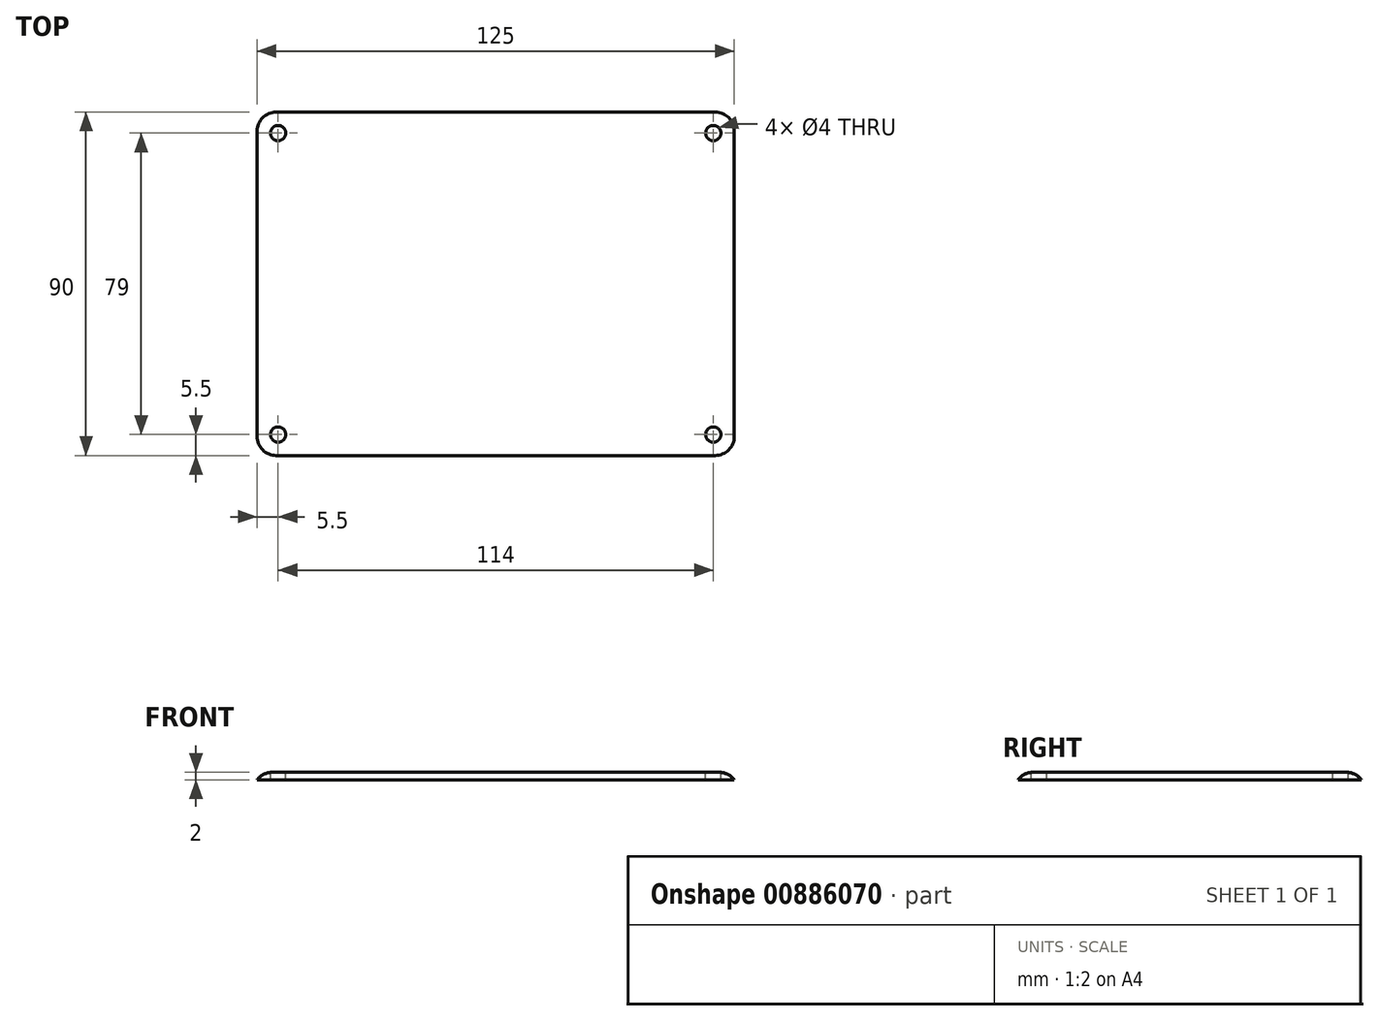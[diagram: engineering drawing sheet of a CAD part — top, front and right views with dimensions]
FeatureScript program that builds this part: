
annotation { "Feature Type Name" : "Feature", "Feature Type Description" : "" }
export const myFeature = defineFeature(function(context is Context, id is Id, definition is map)
    precondition{}
    {
        {
            var Q0;
            Q0=qCreatedBy(makeId("Top.planeOp"),FACE);
            var sketch = newSketch(context, id + "F0", { "sketchPlane" : qUnion([Q0])});
            skLineSegment(sketch, "E0.bottom", {"start": v(62.5, -45) * mm, "end": v(-62.5, -45) * mm});
            skLineSegment(sketch, "E0.top", {"start": v(62.5, 45) * mm, "end": v(-62.5, 45) * mm});
            skLineSegment(sketch, "E0.left", {"start": v(62.5, -45) * mm, "end": v(62.5, 45) * mm});
            skLineSegment(sketch, "E0.right", {"start": v(-62.5, -45) * mm, "end": v(-62.5, 45) * mm});
            skPoint(sketch, "E0.middle", {"position": v(0, 0) * mm});
            skLineSegment(sketch, "E1.bottom", {"start": v(-62.5, 45) * mm, "end": v(-51.5, 45) * mm});
            skLineSegment(sketch, "E1.top", {"start": v(-62.5, 34) * mm, "end": v(-51.5, 34) * mm});
            skLineSegment(sketch, "E1.left", {"start": v(-62.5, 45) * mm, "end": v(-62.5, 34) * mm});
            skLineSegment(sketch, "E1.right", {"start": v(-51.5, 45) * mm, "end": v(-51.5, 34) * mm});
            skLineSegment(sketch, "E2.bottom", {"start": v(-62.5, -45) * mm, "end": v(-51.5, -45) * mm});
            skLineSegment(sketch, "E2.top", {"start": v(-62.5, -34) * mm, "end": v(-51.5, -34) * mm});
            skLineSegment(sketch, "E2.left", {"start": v(-62.5, -45) * mm, "end": v(-62.5, -34) * mm});
            skLineSegment(sketch, "E2.right", {"start": v(-51.5, -45) * mm, "end": v(-51.5, -34) * mm});
            skLineSegment(sketch, "E3.bottom", {"start": v(62.5, -45) * mm, "end": v(51.5, -45) * mm});
            skLineSegment(sketch, "E3.top", {"start": v(62.5, -34) * mm, "end": v(51.5, -34) * mm});
            skLineSegment(sketch, "E3.left", {"start": v(62.5, -45) * mm, "end": v(62.5, -34) * mm});
            skLineSegment(sketch, "E3.right", {"start": v(51.5, -45) * mm, "end": v(51.5, -34) * mm});
            skLineSegment(sketch, "E4.bottom", {"start": v(62.5, 45) * mm, "end": v(51.5, 45) * mm});
            skLineSegment(sketch, "E4.top", {"start": v(62.5, 34) * mm, "end": v(51.5, 34) * mm});
            skLineSegment(sketch, "E4.left", {"start": v(62.5, 45) * mm, "end": v(62.5, 34) * mm});
            skLineSegment(sketch, "E4.right", {"start": v(51.5, 45) * mm, "end": v(51.5, 34) * mm});
            skLineSegment(sketch, "E5", {"start": v(-51.5, -43) * mm, "end": v(51.5, -43) * mm});
            skLineSegment(sketch, "E6", {"start": v(-60.5, -34) * mm, "end": v(-60.5, 34) * mm});
            skLineSegment(sketch, "E7", {"start": v(-51.5, 43) * mm, "end": v(51.5, 43) * mm});
            skLineSegment(sketch, "E8", {"start": v(60.5, -34) * mm, "end": v(60.5, 34) * mm});
            skSolve(sketch);
        }
        {
            var Q0;
            {var subQ0=sQuery(id+"F0.wireOp",EDGE,"E5");Q0=makeQuery(id+"F0.imprint","IMPRINT",FACE,{"disambiguationData":[TD([[makeQuery(id+"F0.imprint","IMPRINT",EDGE,{"derivedFrom":subQ0}),1.0]])]});}
            extrude(context, id + "F1", {"entities" : qUnion([Q0]), "depth" : 2 * mm, "offsetDistance" : 25 * mm});
        }
        {
            var Q0;
            {var subQ4=sQuery(id+"F0.wireOp",EDGE,"E0.right");var subQ5=sQuery(id+"F0.wireOp",EDGE,"E0.bottom");var subQ6=makeQuery(id+"F0.imprint","INTERSECT",VERTEX,{"derivedFrom":[subQ5,subQ4]});Q0=makeQuery(id+"F0.imprint","IMPRINT",FACE,{"disambiguationData":[TD([[makeQuery(id+"F0.imprint","IMPRINT",EDGE,{"disambiguationData":[TD([[subQ6,1.0]])],"derivedFrom":subQ5}),-1.0]])]});}
            var Q1;
            {var subQ5=sQuery(id+"F0.wireOp",EDGE,"E6");Q1=makeQuery(id+"F0.imprint","IMPRINT",FACE,{"disambiguationData":[TD([[makeQuery(id+"F0.imprint","IMPRINT",EDGE,{"derivedFrom":subQ5}),1.0]])]});}
            var Q2;
            {var subQ5=sQuery(id+"F0.wireOp",EDGE,"E5");Q2=makeQuery(id+"F0.imprint","IMPRINT",FACE,{"disambiguationData":[TD([[makeQuery(id+"F0.imprint","IMPRINT",EDGE,{"derivedFrom":subQ5}),-1.0]])]});}
            var Q3;
            {var subQ2=sQuery(id+"F0.wireOp",EDGE,"E3.right");var subQ6=sQuery(id+"F0.wireOp",EDGE,"E0.bottom");var subQ8=makeQuery(id+"F0.imprint","INTERSECT",VERTEX,{"derivedFrom":[subQ6,subQ2]});Q3=makeQuery(id+"F0.imprint","IMPRINT",FACE,{"disambiguationData":[TD([[makeQuery(id+"F0.imprint","IMPRINT",EDGE,{"disambiguationData":[TD([[subQ8,1.0]])],"derivedFrom":subQ6}),-1.0]])]});}
            var Q4;
            {var subQ5=sQuery(id+"F0.wireOp",EDGE,"E8");Q4=makeQuery(id+"F0.imprint","IMPRINT",FACE,{"disambiguationData":[TD([[makeQuery(id+"F0.imprint","IMPRINT",EDGE,{"derivedFrom":subQ5}),-1.0]])]});}
            var Q5;
            {var subQ2=sQuery(id+"F0.wireOp",EDGE,"E4.right");var subQ5=sQuery(id+"F0.wireOp",EDGE,"E0.top");var subQ8=makeQuery(id+"F0.imprint","INTERSECT",VERTEX,{"derivedFrom":[subQ5,subQ2]});Q5=makeQuery(id+"F0.imprint","IMPRINT",FACE,{"disambiguationData":[TD([[makeQuery(id+"F0.imprint","IMPRINT",EDGE,{"disambiguationData":[TD([[subQ8,1.0]])],"derivedFrom":subQ5}),1.0]])]});}
            var Q6;
            {var subQ5=sQuery(id+"F0.wireOp",EDGE,"E7");Q6=makeQuery(id+"F0.imprint","IMPRINT",FACE,{"disambiguationData":[TD([[makeQuery(id+"F0.imprint","IMPRINT",EDGE,{"derivedFrom":subQ5}),1.0]])]});}
            var Q7;
            {var subQ2=sQuery(id+"F0.wireOp",EDGE,"E0.right");var subQ6=sQuery(id+"F0.wireOp",EDGE,"E0.top");var subQ7=makeQuery(id+"F0.imprint","INTERSECT",VERTEX,{"derivedFrom":[subQ6,subQ2]});Q7=makeQuery(id+"F0.imprint","IMPRINT",FACE,{"disambiguationData":[TD([[makeQuery(id+"F0.imprint","IMPRINT",EDGE,{"disambiguationData":[TD([[subQ7,1.0]])],"derivedFrom":subQ6}),1.0]])]});}
            extrude(context, id + "F2", {"entities" : qUnion([Q0, Q1, Q2, Q3, Q4, Q5, Q6, Q7]), "operationType" : NewBodyOperationType.ADD, "depth" : 2 * mm, "offsetDistance" : 25 * mm});
        }
        {
            var Q0;
            {var subQ0=sQuery(id+"F0.wireOp",EDGE,"E8");var subQ1=sQuery(id+"F0.wireOp",EDGE,"E7");var subQ2=sQuery(id+"F0.wireOp",EDGE,"E6");var subQ3=sQuery(id+"F0.wireOp",EDGE,"E5");var subQ4=sQuery(id+"F0.wireOp",EDGE,"E4.right");var subQ5=sQuery(id+"F0.wireOp",EDGE,"E4.top");var subQ6=sQuery(id+"F0.wireOp",EDGE,"E3.right");var subQ7=sQuery(id+"F0.wireOp",EDGE,"E3.top");var subQ8=sQuery(id+"F0.wireOp",EDGE,"E2.right");var subQ9=sQuery(id+"F0.wireOp",EDGE,"E2.top");var subQ10=sQuery(id+"F0.wireOp",EDGE,"E1.right");var subQ11=sQuery(id+"F0.wireOp",EDGE,"E1.top");Q0=makeQuery(id+"F2.boolean.opBoolean","MERGE",FACE,{"derivedFrom":[makeQuery(id+"F1.opExtrude","CAP_FACE",FACE,{"disambiguationData":[OSD([subQ11,subQ10,subQ9,subQ8,subQ7,subQ6,subQ5,subQ4,subQ3,subQ2,subQ1,subQ0])],"isStart":false}),makeQuery(id+"F2.opExtrude","CAP_FACE",FACE,{"disambiguationData":[OSD([sQuery(id+"F0.wireOp",EDGE,"E0.bottom"),sQuery(id+"F0.wireOp",EDGE,"E0.top"),sQuery(id+"F0.wireOp",EDGE,"E0.left"),sQuery(id+"F0.wireOp",EDGE,"E0.right"),subQ11,subQ10,subQ9,subQ8,subQ7,subQ6,subQ5,subQ4,subQ3,subQ2,subQ1,subQ0])],"isStart":false})]});}
            var sketch = newSketch(context, id + "F3", { "sketchPlane" : qUnion([Q0])});
            skLineSegment(sketch, "E9", {"start": v(-51.5, -34) * mm, "end": v(-62.5, -34) * mm, "construction": true});
            skLineSegment(sketch, "E10", {"start": v(-51.5, -34) * mm, "end": v(-51.5, -45) * mm, "construction": true});
            skCircle(sketch, "E11.cCircle", {"center": v(-57, -39.5) * mm, "radius": 3.45 * mm, "construction": true});
            skPoint(sketch, "E11.cCircle.centerSnap0", {"position": v(-57, -34) * mm});
            skPoint(sketch, "E11.cCircle.centerSnap1", {"position": v(-51.5, -39.5) * mm});
            skLineSegment(sketch, "E11.0", {"start": v(-59, -36.05) * mm, "end": v(-55, -36.05) * mm});
            skLineSegment(sketch, "E11.1", {"start": v(-55, -36.05) * mm, "end": v(-53.02, -39.5) * mm});
            skLineSegment(sketch, "E11.2", {"start": v(-53.02, -39.5) * mm, "end": v(-55, -42.95) * mm});
            skLineSegment(sketch, "E11.3", {"start": v(-55, -42.95) * mm, "end": v(-59, -42.95) * mm});
            skLineSegment(sketch, "E11.4", {"start": v(-59, -42.95) * mm, "end": v(-60.98, -39.5) * mm});
            skLineSegment(sketch, "E11.5", {"start": v(-60.98, -39.5) * mm, "end": v(-59, -36.05) * mm});
            skPoint(sketch, "E11.0.midPoint", {"position": v(-57, -36.05) * mm});
            skLineSegment(sketch, "E12", {"start": v(51.5, -34) * mm, "end": v(51.5, -45) * mm, "construction": true});
            skLineSegment(sketch, "E13", {"start": v(51.5, -34) * mm, "end": v(62.5, -34) * mm, "construction": true});
            skCircle(sketch, "E14.cCircle", {"center": v(57, -39.5) * mm, "radius": 3.45 * mm, "construction": true});
            skPoint(sketch, "E14.cCircle.centerSnap0", {"position": v(51.5, -39.5) * mm});
            skPoint(sketch, "E14.cCircle.centerSnap1", {"position": v(57, -34) * mm});
            skLineSegment(sketch, "E14.0", {"start": v(55, -36.05) * mm, "end": v(59, -36.05) * mm});
            skLineSegment(sketch, "E14.1", {"start": v(59, -36.05) * mm, "end": v(60.98, -39.5) * mm});
            skLineSegment(sketch, "E14.2", {"start": v(60.98, -39.5) * mm, "end": v(59, -42.95) * mm});
            skLineSegment(sketch, "E14.3", {"start": v(59, -42.95) * mm, "end": v(55, -42.95) * mm});
            skLineSegment(sketch, "E14.4", {"start": v(55, -42.95) * mm, "end": v(53.02, -39.5) * mm});
            skLineSegment(sketch, "E14.5", {"start": v(53.02, -39.5) * mm, "end": v(55, -36.05) * mm});
            skPoint(sketch, "E14.0.midPoint", {"position": v(57, -36.05) * mm});
            skLineSegment(sketch, "E15", {"start": v(51.5, 34) * mm, "end": v(51.5, 45) * mm, "construction": true});
            skLineSegment(sketch, "E16", {"start": v(51.5, 34) * mm, "end": v(62.5, 34) * mm, "construction": true});
            skLineSegment(sketch, "E17", {"start": v(-51.5, 34) * mm, "end": v(-51.5, 45) * mm, "construction": true});
            skLineSegment(sketch, "E18", {"start": v(-51.5, 34) * mm, "end": v(-62.5, 34) * mm, "construction": true});
            skCircle(sketch, "E19.cCircle", {"center": v(-57, 39.5) * mm, "radius": 3.45 * mm, "construction": true});
            skPoint(sketch, "E19.cCircle.centerSnap0", {"position": v(-57, 34) * mm});
            skPoint(sketch, "E19.cCircle.centerSnap1", {"position": v(-51.5, 39.5) * mm});
            skLineSegment(sketch, "E19.0", {"start": v(-55, 36.05) * mm, "end": v(-59, 36.05) * mm});
            skLineSegment(sketch, "E19.1", {"start": v(-59, 36.05) * mm, "end": v(-60.98, 39.5) * mm});
            skLineSegment(sketch, "E19.2", {"start": v(-60.98, 39.5) * mm, "end": v(-59, 42.95) * mm});
            skLineSegment(sketch, "E19.3", {"start": v(-59, 42.95) * mm, "end": v(-55, 42.95) * mm});
            skLineSegment(sketch, "E19.4", {"start": v(-55, 42.95) * mm, "end": v(-53.02, 39.5) * mm});
            skLineSegment(sketch, "E19.5", {"start": v(-53.02, 39.5) * mm, "end": v(-55, 36.05) * mm});
            skPoint(sketch, "E19.0.midPoint", {"position": v(-57, 36.05) * mm});
            skCircle(sketch, "E20.cCircle", {"center": v(57, 39.5) * mm, "radius": 3.45 * mm, "construction": true});
            skPoint(sketch, "E20.cCircle.centerSnap0", {"position": v(57, 34) * mm});
            skPoint(sketch, "E20.cCircle.centerSnap1", {"position": v(51.5, 39.5) * mm});
            skLineSegment(sketch, "E20.0", {"start": v(59, 36.05) * mm, "end": v(55, 36.05) * mm});
            skLineSegment(sketch, "E20.1", {"start": v(55, 36.05) * mm, "end": v(53.02, 39.5) * mm});
            skLineSegment(sketch, "E20.2", {"start": v(53.02, 39.5) * mm, "end": v(55, 42.95) * mm});
            skLineSegment(sketch, "E20.3", {"start": v(55, 42.95) * mm, "end": v(59, 42.95) * mm});
            skLineSegment(sketch, "E20.4", {"start": v(59, 42.95) * mm, "end": v(60.98, 39.5) * mm});
            skLineSegment(sketch, "E20.5", {"start": v(60.98, 39.5) * mm, "end": v(59, 36.05) * mm});
            skPoint(sketch, "E20.0.midPoint", {"position": v(57, 36.05) * mm});
            skCircle(sketch, "E21", {"center": v(-57, 39.5) * mm, "radius": 3.45 * mm});
            skCircle(sketch, "E22", {"center": v(-57, 39.5) * mm, "radius": 2 * mm});
            skCircle(sketch, "E23", {"center": v(57, 39.5) * mm, "radius": 2 * mm});
            skCircle(sketch, "E24", {"center": v(57, -39.5) * mm, "radius": 2 * mm});
            skCircle(sketch, "E25", {"center": v(-57, -39.5) * mm, "radius": 2 * mm});
            skSolve(sketch);
        }
        {
            var Q0;
            Q0=makeQuery(id+"F3.imprint","IMPRINT",FACE,{"disambiguationData":[TD([[makeQuery(id+"F3.imprint","IMPRINT",EDGE,{"derivedFrom":sQuery(id+"F3.wireOp",EDGE,"E25")}),1.0]])]});
            var Q1;
            Q1=makeQuery(id+"F3.imprint","IMPRINT",FACE,{"disambiguationData":[TD([[makeQuery(id+"F3.imprint","IMPRINT",EDGE,{"derivedFrom":sQuery(id+"F3.wireOp",EDGE,"E24")}),1.0]])]});
            var Q2;
            Q2=makeQuery(id+"F3.imprint","IMPRINT",FACE,{"disambiguationData":[TD([[makeQuery(id+"F3.imprint","IMPRINT",EDGE,{"derivedFrom":sQuery(id+"F3.wireOp",EDGE,"E22")}),1.0]])]});
            var Q3;
            Q3=makeQuery(id+"F3.imprint","IMPRINT",FACE,{"disambiguationData":[TD([[makeQuery(id+"F3.imprint","IMPRINT",EDGE,{"derivedFrom":sQuery(id+"F3.wireOp",EDGE,"E23")}),1.0]])]});
            extrude(context, id + "F4", {"entities" : qUnion([Q0, Q1, Q2, Q3]), "operationType" : NewBodyOperationType.REMOVE, "oppositeDirection" : true, "depth" : 5 * mm, "offsetDistance" : 25 * mm});
        }
        {
            var Q0;
            Q0=makeQuery(id+"F2.opExtrude","SWEPT_EDGE",EDGE,{"disambiguationData":[OSD([sQuery(id+"F0.wireOp",EDGE,"E0.top"),sQuery(id+"F0.wireOp",EDGE,"E0.right")])]});
            var Q1;
            Q1=makeQuery(id+"F2.opExtrude","SWEPT_EDGE",EDGE,{"disambiguationData":[OSD([sQuery(id+"F0.wireOp",EDGE,"E0.top"),sQuery(id+"F0.wireOp",EDGE,"E0.left")])]});
            var Q2;
            Q2=makeQuery(id+"F2.opExtrude","SWEPT_EDGE",EDGE,{"disambiguationData":[OSD([sQuery(id+"F0.wireOp",EDGE,"E0.bottom"),sQuery(id+"F0.wireOp",EDGE,"E0.left")])]});
            var Q3;
            Q3=makeQuery(id+"F2.opExtrude","SWEPT_EDGE",EDGE,{"disambiguationData":[OSD([sQuery(id+"F0.wireOp",EDGE,"E0.bottom"),sQuery(id+"F0.wireOp",EDGE,"E0.right")])]});
            fillet(context, id + "F5", {"entities" : qUnion([Q0, Q1, Q2, Q3]), "radius" : 5 * mm, "tangentPropagation" : true, "allowEdgeOverflow" : false});
        }
        {
            var Q0;
            Q0=makeQuery(id+"F2.opExtrude","CAP_EDGE",EDGE,{"disambiguationData":[OSD([sQuery(id+"F0.wireOp",EDGE,"E0.right")])],"isStart":false});
            fillet(context, id + "F6", {"entities" : qUnion([Q0]), "radius" : 5 * mm, "tangentPropagation" : true, "allowEdgeOverflow" : false});
        }
    });
